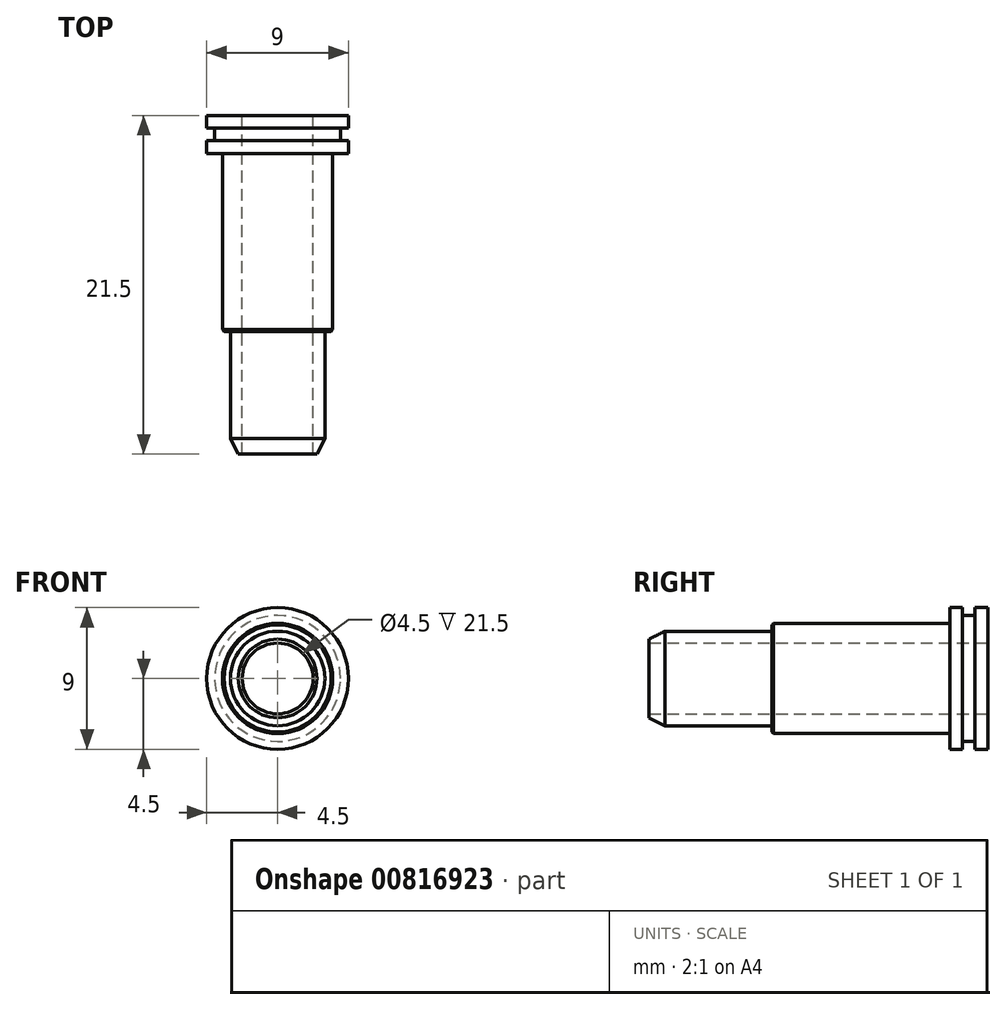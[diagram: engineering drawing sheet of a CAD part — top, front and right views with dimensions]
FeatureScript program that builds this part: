
annotation { "Feature Type Name" : "Feature", "Feature Type Description" : "" }
export const myFeature = defineFeature(function(context is Context, id is Id, definition is map)
    precondition{}
    {
        {
            var Q0;
            Q0=qCreatedBy(makeId("Right.planeOp"),FACE);
            var sketch = newSketch(context, id + "F0", { "sketchPlane" : qUnion([Q0])});
            skLineSegment(sketch, "E0", {"start": v(0, 2.25) * mm, "end": v(0, 4.5) * mm});
            skLineSegment(sketch, "E1", {"start": v(0, 4.5) * mm, "end": v(-0.8, 4.5) * mm});
            skLineSegment(sketch, "E2", {"start": v(-0.8, 4.5) * mm, "end": v(-0.8, 4) * mm});
            skLineSegment(sketch, "E3", {"start": v(-0.8, 4) * mm, "end": v(-1.6, 4) * mm});
            skLineSegment(sketch, "E4", {"start": v(-1.6, 4) * mm, "end": v(-1.6, 4.5) * mm});
            skLineSegment(sketch, "E5", {"start": v(-1.6, 4.5) * mm, "end": v(-2.4, 4.5) * mm});
            skLineSegment(sketch, "E6", {"start": v(-2.4, 4.5) * mm, "end": v(-2.4, 3.5) * mm});
            skLineSegment(sketch, "E7", {"start": v(0, 2.25) * mm, "end": v(-21.5, 2.25) * mm});
            skPoint(sketch, "E8.orphan", {"position": v(0, 0) * mm});
            skPoint(sketch, "E9.orphan", {"position": v(-21.5, 0) * mm});
            skLineSegment(sketch, "E10", {"start": v(0, 0) * mm, "end": v(-21.5, 0) * mm});
            skLineSegment(sketch, "E11", {"start": v(-21.5, 2.25) * mm, "end": v(-21.5, 2.5) * mm});
            skLineSegment(sketch, "E12", {"start": v(-21.5, 2.5) * mm, "end": v(-20.5, 3) * mm});
            skLineSegment(sketch, "E13", {"start": v(-20.5, 3) * mm, "end": v(-13.7, 3) * mm});
            skLineSegment(sketch, "E14", {"start": v(-13.7, 3) * mm, "end": v(-13.7, 3.5) * mm});
            skLineSegment(sketch, "E15", {"start": v(-13.7, 3.5) * mm, "end": v(-2.4, 3.5) * mm});
            skPoint(sketch, "E16.orphan", {"position": v(-2.4, 3) * mm});
            skSolve(sketch);
        }
        {
            var Q0;
            Q0 = qSketchRegion(id + "F0", true);
            var Q1;
            Q1=sQuery(id+"F0.wireOp",EDGE,"E10");
            revolve(context, id + "F1", {"surfaceOperationType" : NewSurfaceOperationType.NEW, "entities" : qUnion([Q0]), "axis" : qUnion([Q1]), "revolveType" : RevolveType.FULL});
        }
        {
            var Q0;
            Q0=makeQuery(id+"F1.opRevolve","SWEPT_EDGE",EDGE,{"disambiguationData":[OSD([sQuery(id+"F0.wireOp",EDGE,"E14"),sQuery(id+"F0.wireOp",EDGE,"E15")])]});
            chamfer(context, id + "F2", {"entities" : qUnion([Q0]), "width" : 0.1 * mm, "tangentPropagation" : true});
        }
    });
